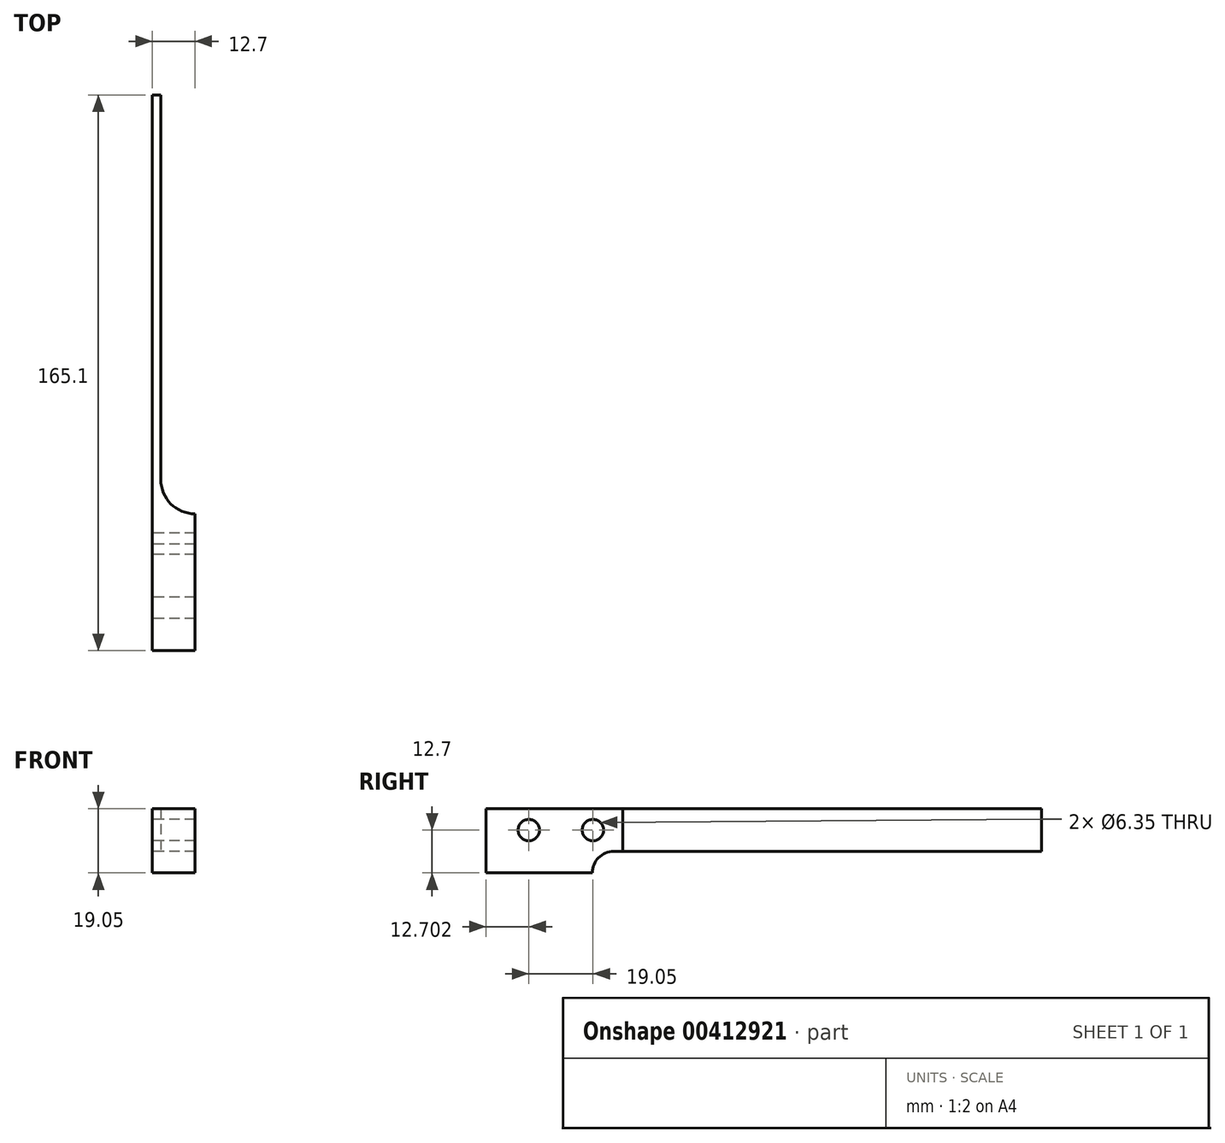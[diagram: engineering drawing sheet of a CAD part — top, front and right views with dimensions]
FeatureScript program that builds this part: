
annotation { "Feature Type Name" : "Feature", "Feature Type Description" : "" }
export const myFeature = defineFeature(function(context is Context, id is Id, definition is map)
    precondition{}
    {
        {
            var Q0;
            Q0=qCreatedBy(makeId("Top.planeOp"),FACE);
            var sketch = newSketch(context, id + "F0", { "sketchPlane" : qUnion([Q0])});
            skLineSegment(sketch, "E0.bottom", {"start": v(33.45, 94.37) * mm, "end": v(46.15, 94.37) * mm});
            skLineSegment(sketch, "E0.top", {"start": v(33.45, -70.73) * mm, "end": v(46.15, -70.73) * mm});
            skLineSegment(sketch, "E0.left", {"start": v(33.45, 94.37) * mm, "end": v(33.45, -70.73) * mm});
            skLineSegment(sketch, "E0.right", {"start": v(46.15, 94.37) * mm, "end": v(46.15, -70.73) * mm});
            skLineSegment(sketch, "E1", {"start": v(36, 94.37) * mm, "end": v(36, -19.93) * mm});
            skLineSegment(sketch, "E2", {"start": v(36, -19.93) * mm, "end": v(33.45, -19.93) * mm, "construction": true});
            skLineSegment(sketch, "E3", {"start": v(39.8, 94.37) * mm, "end": v(39.8, -70.73) * mm, "construction": true});
            skLineSegment(sketch, "E4", {"start": v(36, -19.93) * mm, "end": v(46.15, -19.93) * mm, "construction": true});
            skArc(sketch, "E5", {"start": v(36, -19.93) * mm, "mid": v(38.97, -27.11) * mm, "end": v(46.15, -30.09) * mm});
            skSolve(sketch);
        }
        {
            var Q0;
            {var subQ2=sQuery(id+"F0.wireOp",EDGE,"E0.top");Q0=makeQuery(id+"F0.imprint","IMPRINT",FACE,{"disambiguationData":[TD([[makeQuery(id+"F0.imprint","IMPRINT",EDGE,{"derivedFrom":subQ2}),1.0]])]});}
            extrude(context, id + "F1", {"entities" : qUnion([Q0]), "depth" : 12.7 * mm});
        }
        {
            var Q0;
            Q0=makeQuery(id+"F1.opExtrude","SWEPT_FACE",FACE,{"disambiguationData":[OSD([sQuery(id+"F0.wireOp",EDGE,"E0.left")])]});
            var sketch = newSketch(context, id + "F2", { "sketchPlane" : qUnion([Q0])});
            skLineSegment(sketch, "E6", {"start": v(-94.37, 6.35) * mm, "end": v(70.73, 6.35) * mm, "construction": true});
            skCircle(sketch, "E7", {"center": v(58.03, 6.35) * mm, "radius": 3.18 * mm});
            skCircle(sketch, "E8", {"center": v(38.98, 6.35) * mm, "radius": 3.18 * mm});
            skSolve(sketch);
        }
        {
            var Q0;
            Q0 = qSketchRegion(id + "F2", true);
            extrude(context, id + "F3", {"entities" : qUnion([Q0]), "operationType" : NewBodyOperationType.REMOVE, "oppositeDirection" : true, "depth" : 25.4 * mm});
        }
        {
            var Q0;
            Q0=makeQuery(id+"F1.opExtrude","CAP_FACE",FACE,{"disambiguationData":[OSD([sQuery(id+"F0.wireOp",EDGE,"E0.bottom"),sQuery(id+"F0.wireOp",EDGE,"E0.top"),sQuery(id+"F0.wireOp",EDGE,"E0.left"),sQuery(id+"F0.wireOp",EDGE,"E0.right"),sQuery(id+"F0.wireOp",EDGE,"E1"),sQuery(id+"F0.wireOp",EDGE,"E5")])],"isStart":true});
            extrude(context, id + "F4", {"entities" : qUnion([Q0]), "operationType" : NewBodyOperationType.ADD, "depth" : 6.35 * mm});
        }
        {
            var Q0;
            {var subQ0=sQuery(id+"F0.wireOp",EDGE,"E0.left");Q0=makeQuery(id+"F4.boolean.opBoolean","MERGE",FACE,{"derivedFrom":[makeQuery(id+"F1.opExtrude","SWEPT_FACE",FACE,{"disambiguationData":[OSD([subQ0])]}),makeQuery(id+"F4.opExtrude","SWEPT_FACE",FACE,{"disambiguationData":[OSD([subQ0])]})]});}
            var sketch = newSketch(context, id + "F5", { "sketchPlane" : qUnion([Q0])});
            skLineSegment(sketch, "E9", {"start": v(-94.37, 0) * mm, "end": v(32.8, 0) * mm});
            skArc(sketch, "E10", {"start": v(32.8, 0) * mm, "mid": v(37.3, -1.86) * mm, "end": v(39.16, -6.35) * mm});
            skSolve(sketch);
        }
        {
            var Q0;
            Q0 = qSketchRegion(id + "F5", true);
            var Q1;
            {var subQ0=sQuery(id+"F5.wireOp",EDGE,"E9");Q1=makeQuery(id+"F5.imprint","IMPRINT",FACE,{"disambiguationData":[TD([[makeQuery(id+"F5.imprint","IMPRINT",EDGE,{"derivedFrom":subQ0}),-1.0]])]});}
            extrude(context, id + "F6", {"entities" : qUnion([Q0, Q1]), "operationType" : NewBodyOperationType.REMOVE, "oppositeDirection" : true, "depth" : 25.4 * mm});
        }
    });
